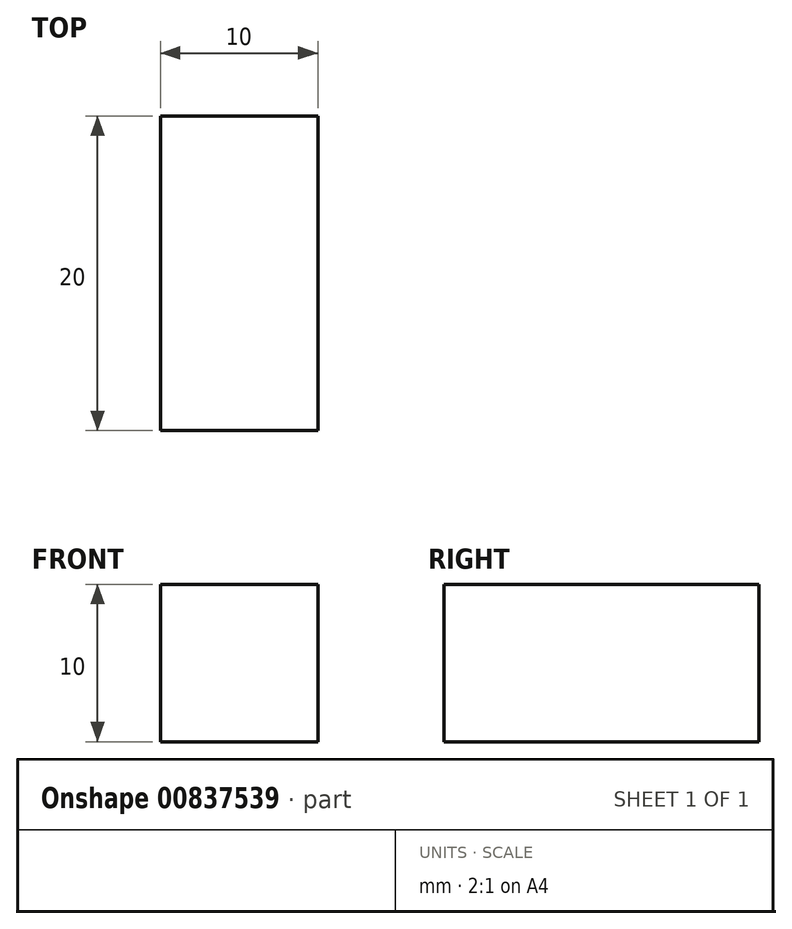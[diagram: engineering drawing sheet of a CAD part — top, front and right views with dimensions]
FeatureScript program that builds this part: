
annotation { "Feature Type Name" : "Feature", "Feature Type Description" : "" }
export const myFeature = defineFeature(function(context is Context, id is Id, definition is map)
    precondition{}
    {
        {
            var Q0;
            Q0=qCreatedBy(makeId("Front.planeOp"),FACE);
            var sketch = newSketch(context, id + "F0", { "sketchPlane" : qUnion([Q0])});
            skLineSegment(sketch, "E0.bottom", {"start": v(-6.37, 4.6) * mm, "end": v(3.63, 4.6) * mm});
            skLineSegment(sketch, "E0.top", {"start": v(-6.37, -5.4) * mm, "end": v(3.63, -5.4) * mm});
            skLineSegment(sketch, "E0.left", {"start": v(-6.37, 4.6) * mm, "end": v(-6.37, -5.4) * mm});
            skLineSegment(sketch, "E0.right", {"start": v(3.63, 4.6) * mm, "end": v(3.63, -5.4) * mm});
            skSolve(sketch);
        }
        {
            var Q0;
            Q0=makeQuery(id+"F0.imprint","IMPRINT",FACE,{"disambiguationData":[TD([[makeQuery(id+"F0.imprint","IMPRINT",EDGE,{"derivedFrom":sQuery(id+"F0.wireOp",EDGE,"E0.bottom")}),-1.0]])]});
            extrude(context, id + "F1", {"entities" : qUnion([Q0]), "depth" : 20 * mm, "offsetDistance" : 25 * mm});
        }
    });
